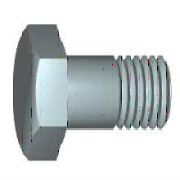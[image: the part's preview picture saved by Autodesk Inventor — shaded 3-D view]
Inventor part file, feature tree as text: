
AUTODESK INVENTOR PART (.ipt)
format: ipt  version: 2023.2 (Build 272271030, 271C)  size: 174,080 bytes
history: native  units: mm
features: sketch x2, revolve x1, thread x1, chamfer x1
ambient origin geometry x8: Origin, YZ Plane, XZ Plane, XY Plane, X Axis, Y Axis, Z Axis, Center Point
bodies: Solid1 (feature_tree)
feature tree (5):
  revolve  "Revolution1"  [1 undecoded]
  thread  "Thread1"  [1 undecoded]
  chamfer  "Chamfer1"  Distance=0.6mm
  sketch  "Sketch1"  dims[d0=19.5mm d1=8.0mm d3=40.0mm]
  sketch  "Sketch2"  dims[d4=11.5mm d5=0.6mm d6=90.0deg d14=22.0mm d15=0.0mm d16=0.666667mm d17=2.0mm d18=45.0deg d19=0.0mm d20=0.0mm d21=0.0mm d22=30.0deg d23=12.35mm d24=5.3mm d25=13.0mm d26=5.3mm d27=0.0mm]
note: 2 required parameter values undecoded (feature->parameter linkage not recoverable at this tier; creation-order binding heuristic only, values carry confidence <= 0.55)